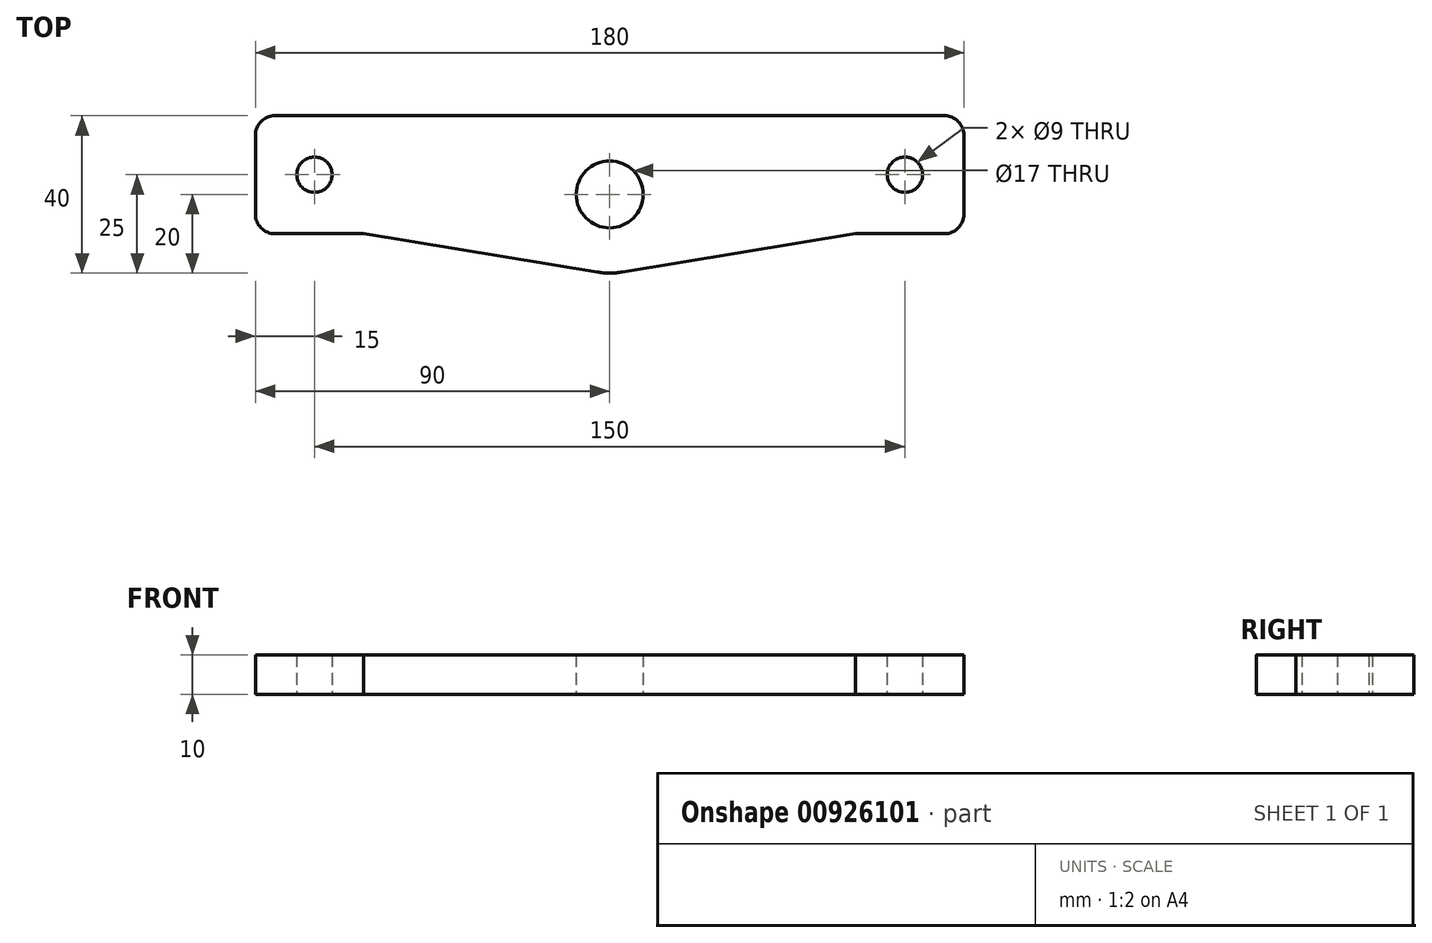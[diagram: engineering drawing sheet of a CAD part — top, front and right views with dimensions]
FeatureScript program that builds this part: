
annotation { "Feature Type Name" : "Feature", "Feature Type Description" : "" }
export const myFeature = defineFeature(function(context is Context, id is Id, definition is map)
    precondition{}
    {
        {
            var Q0;
            Q0=qCreatedBy(makeId("Top.planeOp"),FACE);
            var sketch = newSketch(context, id + "F0", { "sketchPlane" : qUnion([Q0])});
            skLineSegment(sketch, "E0.top", {"start": v(-90, -10) * mm, "end": v(90, -10) * mm});
            skLineSegment(sketch, "E0.left", {"start": v(-90, 20) * mm, "end": v(-90, -10) * mm});
            skLineSegment(sketch, "E0.right", {"start": v(90, 20) * mm, "end": v(90, -10) * mm});
            skPoint(sketch, "E0.middle", {"position": v(0, 0) * mm});
            skCircle(sketch, "E1", {"center": v(0, 0) * mm, "radius": 20 * mm});
            skLineSegment(sketch, "E2", {"start": v(62.5, -10) * mm, "end": v(3.24, -19.74) * mm});
            skLineSegment(sketch, "E3", {"start": v(-3.24, -19.74) * mm, "end": v(-62.5, -10) * mm});
            skCircle(sketch, "E4", {"center": v(0, 0) * mm, "radius": 8.5 * mm});
            skCircle(sketch, "E5", {"center": v(-75, 5) * mm, "radius": 4.5 * mm});
            skCircle(sketch, "E6", {"center": v(75, 5) * mm, "radius": 4.5 * mm});
            skLineSegment(sketch, "E7", {"start": v(-90, 20) * mm, "end": v(90, 20) * mm});
            skSolve(sketch);
        }
        {
            var Q0;
            Q0=qSketchRegion(id+"F0",true);
            var Q1;
            Q1=makeQuery(id+"F0.imprint","IMPRINT",FACE,{"disambiguationData":[TD([[makeQuery(id+"F0.imprint","IMPRINT",EDGE,{"derivedFrom":sQuery(id+"F0.wireOp",EDGE,"E4")}),-1.0]])]});
            extrude(context, id + "F1", {"entities" : qUnion([Q0, Q1]), "depth" : 10 * mm, "offsetDistance" : 25 * mm});
        }
        {
            var Q0;
            Q0=makeQuery(id+"F1.opExtrude","SWEPT_EDGE",EDGE,{"disambiguationData":[OSD([sQuery(id+"F0.wireOp",EDGE,"E0.top"),sQuery(id+"F0.wireOp",EDGE,"E0.left")])]});
            var Q1;
            Q1=makeQuery(id+"F1.opExtrude","SWEPT_EDGE",EDGE,{"disambiguationData":[OSD([sQuery(id+"F0.wireOp",EDGE,"E0.bottom"),sQuery(id+"F0.wireOp",EDGE,"E0.left")])]});
            var Q2;
            Q2=makeQuery(id+"F1.opExtrude","SWEPT_EDGE",EDGE,{"disambiguationData":[OSD([sQuery(id+"F0.wireOp",EDGE,"E0.top"),sQuery(id+"F0.wireOp",EDGE,"E0.right")])]});
            var Q3;
            Q3=makeQuery(id+"F1.opExtrude","SWEPT_EDGE",EDGE,{"disambiguationData":[OSD([sQuery(id+"F0.wireOp",EDGE,"E0.bottom"),sQuery(id+"F0.wireOp",EDGE,"E0.right")])]});
            fillet(context, id + "F2", {"entities" : qUnion([Q0, Q1, Q2, Q3]), "radius" : 5 * mm, "tangentPropagation" : true, "allowEdgeOverflow" : false});
        }
    });
